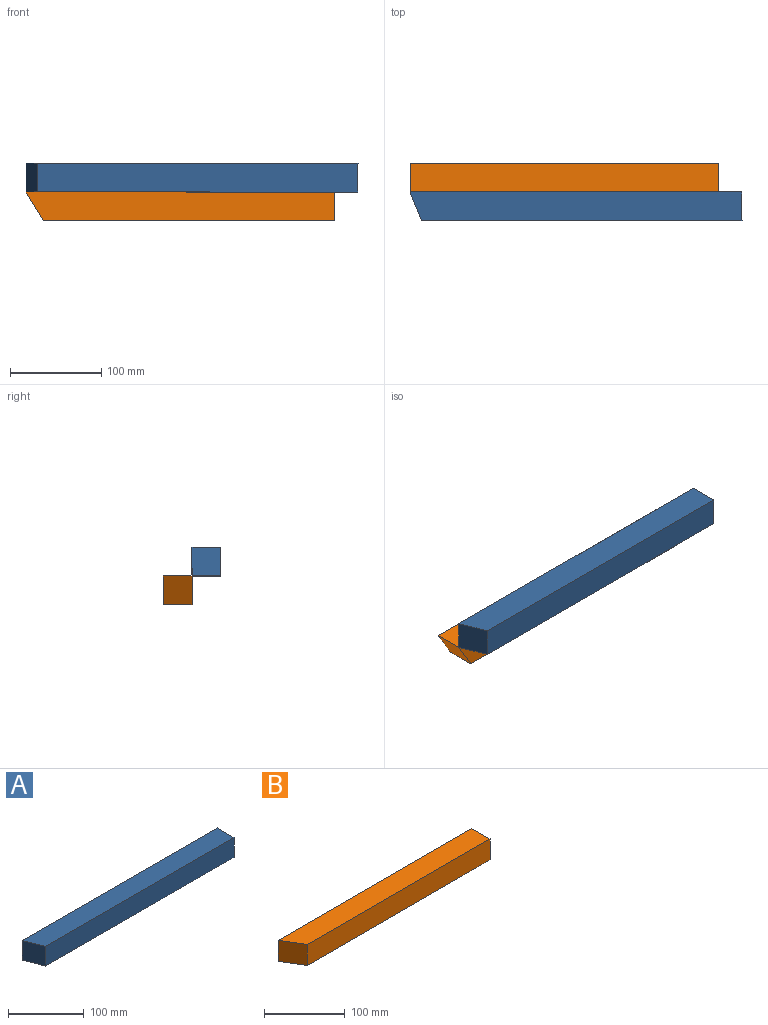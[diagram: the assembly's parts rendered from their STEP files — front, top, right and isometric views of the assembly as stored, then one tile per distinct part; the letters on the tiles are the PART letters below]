
ASSEMBLY  parts=2 mates=1
PART A: 6 faces, bbox 364.5x31.8x31.8 mm
  f0: plane 364.49x31.75mm, normal (0,1,0), area 11572.6mm2, adj f1,f3,f4,f5
  f1: plane 31.75x31.75mm, normal (-0.93,-0.37,0), area 1085.7mm2, adj f0,f2,f3,f4
  f2: plane 351.79x31.75mm, normal (0,-1,0), area 11169.3mm2, adj f1,f3,f4,f5
  f3: plane 364.49x31.75mm, normal (0,0,1), area 11370.9mm2, adj f0,f1,f2,f5
  f4: plane 364.49x31.75mm, normal (0,0,-1), area 11370.9mm2, adj f0,f1,f2,f5
  f5: plane 31.75x31.75mm, normal (1,0,0), area 1008.1mm2, adj f0,f2,f3,f4
PART B: 6 faces, bbox 339.1x31.8x31.8 mm
  f0: plane 339.09x31.75mm, normal (0,1,0), area 10766.1mm2, adj f1,f3,f4,f5
  f1: plane 31.75x31.75mm, normal (-0.86,-0.51,0), area 1175.6mm2, adj f0,f2,f3,f4
  f2: plane 320.04x31.75mm, normal (0,-1,0), area 10161.3mm2, adj f1,f3,f4,f5
  f3: plane 339.09x31.75mm, normal (0,0,1), area 10463.7mm2, adj f0,f1,f2,f5
  f4: plane 339.09x31.75mm, normal (0,0,-1), area 10463.7mm2, adj f0,f1,f2,f5
  f5: plane 31.75x31.75mm, normal (1,0,0), area 1008.1mm2, adj f0,f2,f3,f4
PLACE A rot(axis=(-0.48,0.56,0.68),0deg) t=(75.22,219.81,-25.63)mm
PLACE B rot(axis=(1,0,0),90deg) t=(75.22,251.56,-25.63)mm
MATE revolute B.f0 <-> A.f4  axis (0,0,1) through (75.22,219.81,-25.63)mm
